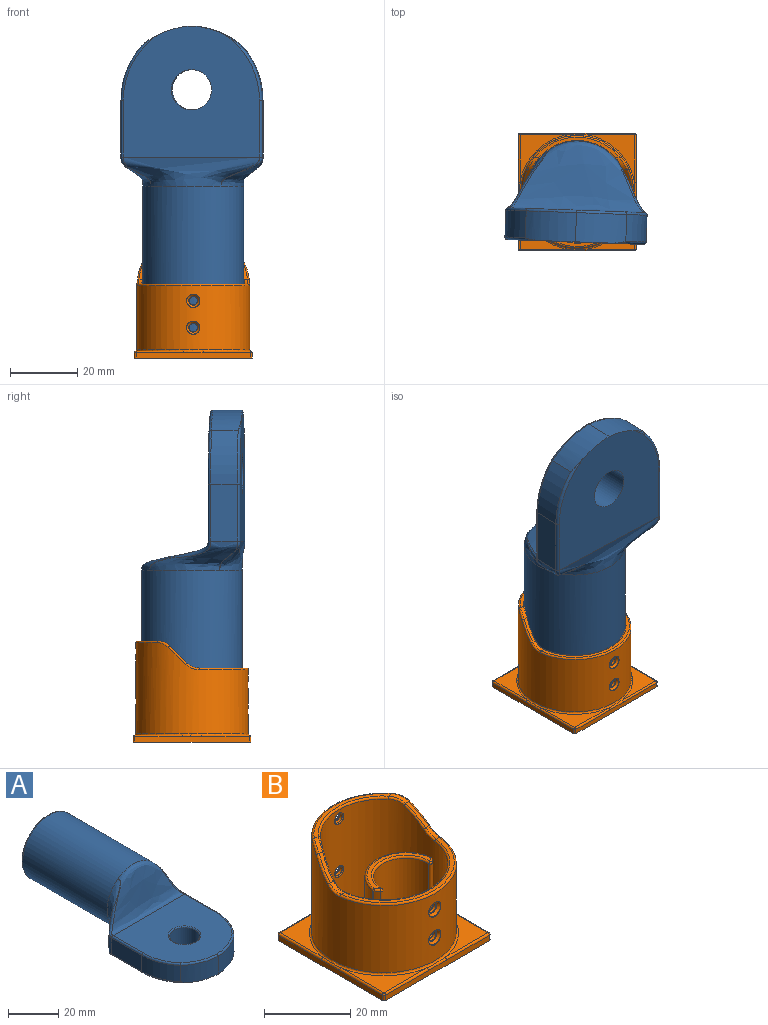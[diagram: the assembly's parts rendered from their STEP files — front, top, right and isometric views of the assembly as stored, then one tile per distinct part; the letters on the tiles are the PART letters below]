
ASSEMBLY  parts=2 mates=1
PART A: 36 faces, bbox 46x98x32.5 mm
  f0: plane 40.51x38.23mm, normal (0,0,1), area 1235.7mm2, adj f8,f9,f10,f11,f12,f13,f19,f29
  f1: plane 40.51x38.98mm, normal (0,0,-1), area 1275.2mm2, adj f5,f6,f14,f15,f16,f17,f18,f31
  f2: plane 16.95x7.94mm, normal (1,0,0), area 134.5mm2, adj f7,f13,f16,f30
  f3: plane 16.95x7.94mm, normal (-1,0,0), area 134.5mm2, adj f4,f8,f14,f28
  f4: cylinder r=24.27mm len=16.02mm, axis (0,0,-1), area 138.9mm2, adj f3,f5,f9,f15
  f5: cylinder r=24.27mm len=14.96mm, axis (0,0,-1), area 140.6mm2, adj f1,f4,f6,f10,f15
  f6: cylinder r=24.27mm len=14.96mm, axis (0,0,-1), area 140.6mm2, adj f1,f5,f7,f11,f17
  f7: cylinder r=24.27mm len=16.02mm, axis (0,0,1), area 138.9mm2, adj f2,f6,f12,f17
  f8: cylinder r=0.75mm len=16.95mm, axis (0,-1,0), area 19.8mm2, adj f0,f3,f9,f33
  f9: torus R=23.53mm, axis (0,0,1), area 20.2mm2, adj f0,f4,f8,f10
  f10: torus R=23.53mm, axis (0,0,1), area 19mm2, adj f0,f5,f9,f11
  f11: torus R=23.53mm, axis (0,0,1), area 19mm2, adj f0,f6,f10,f12
  f12: torus R=23.53mm, axis (0,0,1), area 20.2mm2, adj f0,f7,f11,f13
  f13: cylinder r=0.75mm len=16.95mm, axis (0,1,0), area 19.8mm2, adj f0,f2,f12,f32
  f14: cylinder r=0.75mm len=16.95mm, axis (0,1,0), area 19.8mm2, adj f1,f3,f15,f27,f28,f31
  f15: torus R=23.53mm, axis (0,0,1), area 23.6mm2, adj f1,f4,f5,f14
  f16: cylinder r=0.75mm len=16.95mm, axis (0,-1,0), area 19.8mm2, adj f1,f2,f17,f20,f30,f31
  f17: torus R=23.53mm, axis (0,0,1), area 23.6mm2, adj f1,f6,f7,f16
  f18: cylinder r=6mm len=12mm, axis (0,0,1), area 336.6mm2, adj f1,f19
  f19: torus R=6.5mm, axis (0,0,1), area 30.5mm2, adj f0,f18
  f20: plane 0.77x0.77mm, normal (0,-1,0), area 0mm2, adj f16,f34
  f21: plane 28.51x28.51mm, normal (0,1,0), area 147.8mm2, adj f25,f26
  f22: cylinder r=15mm len=47.63mm, axis (0,1,0), area 4489.2mm2, adj f26,f28,f29,f30,f31
  f23: cylinder r=11.75mm len=44.25mm, axis (0,1,0), area 3267.2mm2, adj f24,f25
  f24: plane 23.5x23.5mm, normal (0,1,0), area 433.7mm2, adj f23
  f25: torus R=12.5mm, axis (0,1,0), area 88.4mm2, adj f21,f23
  f26: torus R=14.25mm, axis (0,1,0), area 108.4mm2, adj f21,f22
  f27: plane 0.77x0.77mm, normal (0,-1,0), area 0mm2, adj f14,f35
  f28: bspline ~27.21x12.28mm, area 160.6mm2, adj f3,f14,f22,f29,f31,f33,f35
  f29: bspline ~42x20.82mm, area 655.7mm2, adj f0,f22,f28,f30,f32,f33
  f30: bspline ~23.72x12.28mm, area 172.3mm2, adj f2,f16,f22,f29,f31,f32,f34
  f31: bspline ~42x8.62mm, area 297.2mm2, adj f1,f14,f16,f22,f28,f30,f34,f35
  f32: bspline ~15.03x8.79mm, area 23.9mm2, adj f13,f29,f30
  f33: bspline ~18.51x12.27mm, area 21.4mm2, adj f8,f28,f29
  f34: bspline ~12.27x8.29mm, area 7.3mm2, adj f20,f30,f31
  f35: bspline ~8.76x8.34mm, area 5.5mm2, adj f27,f28,f31
PART B: 130 faces, bbox 38.1x38.1x30.6 mm
  f0: cylinder r=14.75mm len=29.5mm, axis (0,0,-1), area 2083.4mm2, adj f1,f93,f94,f95,f96,f97,f98,f99
  f1: bspline ~3x2.95mm, area 3.2mm2, adj f0,f2
  f2: cylinder r=1.25mm len=2.5mm, axis (0,1,0), area 6.1mm2, adj f1,f3
  f3: torus R=1.5mm, axis (0,-1,0), area 1.6mm2, adj f2,f4
  f4: cone r=1.25mm half-angle=45deg, axis (0,1,0), area 9.2mm2, adj f3,f5,f88,f89,f90,f91,f92
  f5: bspline ~1.97x1.65mm, area 0.2mm2, adj f4,f6,f92
  f6: cylinder r=16.75mm len=33.5mm, axis (0,0,-1), area 2309.1mm2, adj f5,f7,f13,f14,f15,f16,f17,f18
  f7: cylinder r=2mm len=1.48mm, axis (0,-1,0), area 0mm2, adj f6,f8
  f8: torus R=1.75mm, axis (0,-1,0), area 0.3mm2, adj f7,f9,f13,f17
  f9: cone r=1.25mm half-angle=45deg, axis (0,-1,0), area 9.2mm2, adj f8,f10,f11,f13,f14,f16,f17
  f10: torus R=1.75mm, axis (0,-1,0), area 0.3mm2, adj f9,f14,f15,f16
  f11: torus R=1.5mm, axis (0,1,0), area 1.6mm2, adj f9,f12
  f12: cylinder r=1.25mm len=2.5mm, axis (0,-1,0), area 6.1mm2, adj f11,f95
  f13: bspline ~1.97x1.65mm, area 0.2mm2, adj f6,f8,f9
  f14: bspline ~1.97x1.65mm, area 0.2mm2, adj f6,f9,f10
  f15: cylinder r=2mm len=1.48mm, axis (0,-1,0), area 0mm2, adj f6,f10
  f16: bspline ~1.97x1.65mm, area 0.2mm2, adj f6,f9,f10
  f17: bspline ~1.97x1.65mm, area 0.2mm2, adj f6,f8,f9
  f18: cylinder r=2mm len=1.48mm, axis (0,1,0), area 0mm2, adj f6,f19
  f19: torus R=1.75mm, axis (0,1,0), area 0.3mm2, adj f18,f20,f24,f28
  f20: cone r=1.25mm half-angle=45deg, axis (0,1,0), area 9.2mm2, adj f19,f21,f22,f24,f25,f27,f28
  f21: torus R=1.75mm, axis (0,1,0), area 0.3mm2, adj f20,f25,f26,f27
  f22: torus R=1.5mm, axis (0,-1,0), area 1.6mm2, adj f20,f23
  f23: cylinder r=1.25mm len=2.5mm, axis (0,1,0), area 6.1mm2, adj f22,f93
  f24: bspline ~1.97x1.65mm, area 0.2mm2, adj f6,f19,f20
  f25: bspline ~1.97x1.65mm, area 0.2mm2, adj f6,f20,f21
  f26: cylinder r=2mm len=1.48mm, axis (0,1,0), area 0mm2, adj f6,f21
  f27: bspline ~1.97x1.65mm, area 0.2mm2, adj f6,f20,f21
  f28: bspline ~1.97x1.65mm, area 0.2mm2, adj f6,f19,f20
  f29: cylinder r=2mm len=1.48mm, axis (0,1,0), area 0mm2, adj f6,f89
  f30: cylinder r=2mm len=1.48mm, axis (0,1,0), area 0mm2, adj f6,f92
  f31: cylinder r=2mm len=1.48mm, axis (0,-1,0), area 0mm2, adj f6,f32
  f32: torus R=1.75mm, axis (0,-1,0), area 0.3mm2, adj f31,f33,f37,f41
  f33: cone r=1.25mm half-angle=45deg, axis (0,-1,0), area 9.2mm2, adj f32,f34,f35,f37,f38,f40,f41
  f34: torus R=1.75mm, axis (0,-1,0), area 0.3mm2, adj f33,f38,f39,f40
  f35: torus R=1.5mm, axis (0,1,0), area 1.6mm2, adj f33,f36
  f36: cylinder r=1.25mm len=2.5mm, axis (0,-1,0), area 6.1mm2, adj f35,f94
  f37: bspline ~1.97x1.65mm, area 0.2mm2, adj f6,f32,f33
  f38: bspline ~1.97x1.65mm, area 0.2mm2, adj f6,f33,f34
  f39: cylinder r=2mm len=1.48mm, axis (0,-1,0), area 0mm2, adj f6,f34
  f40: bspline ~1.97x1.65mm, area 0.2mm2, adj f6,f33,f34
  f41: bspline ~1.97x1.65mm, area 0.2mm2, adj f6,f32,f33
  f42: bspline ~10.08x10.01mm, area 6.5mm2, adj f6,f43,f81,f87
  f43: plane 5.07x5.07mm, normal (0,-0.71,0.71), area 7.5mm2, adj f42,f44,f50,f99
  f44: cylinder r=5mm len=3.54mm, axis (-1,0,0), area 4.7mm2, adj f43,f45,f87,f98
  f45: plane 25.51x6.18mm, normal (0,0,1), area 27.6mm2, adj f44,f46,f86,f97
  f46: cylinder r=5mm len=3.54mm, axis (-1,0,0), area 4.7mm2, adj f45,f47,f85,f96
  f47: plane 5.07x5.07mm, normal (0,-0.71,0.71), area 7.5mm2, adj f46,f48,f84,f129
  f48: cylinder r=5mm len=3.54mm, axis (-1,0,0), area 4mm2, adj f47,f49,f83,f128
  f49: plane 32.24x14.18mm, normal (0,0,1), area 45.3mm2, adj f48,f50,f82,f127
  f50: cylinder r=5mm len=3.54mm, axis (-1,0,0), area 4mm2, adj f43,f49,f81,f126
  f51: torus R=17.25mm, axis (0,0,1), area 81.7mm2, adj f6,f52,f74,f75,f76,f77,f78,f79
  f52: plane 14.07x14.07mm, normal (0,0,1), area 56.3mm2, adj f51,f53,f73
  f53: cylinder r=0.5mm len=14.07mm, axis (1,0,0), area 11.1mm2, adj f52,f54,f72,f74
  f54: plane 34x1.53mm, normal (0,1,0), area 51.1mm2, adj f53,f55,f69,f70,f71,f74
  f55: cylinder r=0.5mm len=14.07mm, axis (1,0,0), area 11.1mm2, adj f54,f56,f74,f75
  f56: sphere r=0.5mm, area 0.5mm2, adj f55,f57,f69
  f57: cylinder r=0.5mm len=14.07mm, axis (0,1,0), area 11.1mm2, adj f56,f58,f75,f76
  f58: plane 34x1.53mm, normal (-1,0,0), area 51.1mm2, adj f57,f59,f68,f69,f70,f76
  f59: cylinder r=0.5mm len=14.07mm, axis (0,1,0), area 11.1mm2, adj f58,f60,f76,f77
  f60: sphere r=0.5mm, area 0.4mm2, adj f59,f61,f68
  f61: cylinder r=0.5mm len=14.07mm, axis (-1,0,0), area 11.1mm2, adj f60,f62,f77,f78
  f62: plane 34x1.53mm, normal (0,-1,0), area 51.1mm2, adj f61,f63,f67,f68,f70,f78
  f63: cylinder r=0.5mm len=14.07mm, axis (-1,0,0), area 11.1mm2, adj f62,f64,f78,f79
  f64: sphere r=0.5mm, area 0.4mm2, adj f63,f65,f67
  f65: cylinder r=0.5mm len=14.07mm, axis (0,-1,0), area 11.1mm2, adj f64,f66,f79,f80
  f66: plane 34x1.53mm, normal (1,0,0), area 51.1mm2, adj f65,f67,f70,f71,f73,f80
  f67: cylinder r=0.5mm len=1.5mm, axis (0,0,1), area 1.2mm2, adj f62,f64,f66,f70
  f68: cylinder r=0.5mm len=1.5mm, axis (0,0,-1), area 1.2mm2, adj f58,f60,f62,f70
  f69: cylinder r=0.5mm len=1.5mm, axis (0,0,1), area 1.2mm2, adj f54,f56,f58,f70
  f70: plane 35x35mm, normal (0,0,-1), area 1224.8mm2, adj f54,f58,f62,f66,f67,f68,f69,f71
  f71: cylinder r=0.5mm len=1.5mm, axis (0,0,-1), area 1.2mm2, adj f54,f66,f70,f72
  f72: sphere r=0.5mm, area 0.2mm2, adj f53,f71,f73
  f73: cylinder r=0.5mm len=14.07mm, axis (0,-1,0), area 11.1mm2, adj f52,f66,f72,f80
  f74: bspline ~6.69x0.57mm, area 4.1mm2, adj f51,f53,f54,f55
  f75: plane 14.07x14.07mm, normal (0,0,1), area 56.3mm2, adj f51,f55,f57
  f76: bspline ~8.52x0.68mm, area 4.1mm2, adj f51,f57,f58,f59
  f77: plane 14.07x14.07mm, normal (0,0,1), area 56.3mm2, adj f51,f59,f61
  f78: bspline ~8.52x0.68mm, area 4.1mm2, adj f51,f61,f62,f63
  f79: plane 14.07x14.07mm, normal (0,0,1), area 56.3mm2, adj f51,f63,f65
  f80: bspline ~6.19x0.52mm, area 4.1mm2, adj f51,f65,f66,f73
  f81: bspline ~6.07x2.88mm, area 3.3mm2, adj f6,f42,f50,f82
  f82: torus R=16.25mm, axis (0,0,1), area 37.6mm2, adj f6,f49,f81,f83
  f83: bspline ~6.07x2.88mm, area 3.3mm2, adj f6,f48,f82,f84
  f84: bspline ~10.08x10.01mm, area 6.5mm2, adj f6,f47,f83,f85
  f85: bspline ~4.84x3.15mm, area 3.8mm2, adj f6,f46,f84,f86
  f86: torus R=16.25mm, axis (0,0,1), area 23.5mm2, adj f6,f45,f85,f87
  f87: bspline ~5.75x3.9mm, area 3.8mm2, adj f6,f42,f44,f86
  f88: bspline ~1.97x1.65mm, area 0.2mm2, adj f4,f6,f89
  f89: torus R=1.75mm, axis (0,1,0), area 0.3mm2, adj f4,f29,f88,f90
  f90: bspline ~1.97x1.65mm, area 0.2mm2, adj f4,f6,f89
  f91: bspline ~1.97x1.65mm, area 0.2mm2, adj f4,f6,f92
  f92: torus R=1.75mm, axis (0,1,0), area 0.3mm2, adj f4,f5,f30,f91
  f93: bspline ~3x2.95mm, area 3.2mm2, adj f0,f23
  f94: bspline ~3x2.95mm, area 3.2mm2, adj f0,f36
  f95: bspline ~3x2.95mm, area 3.2mm2, adj f0,f12
  f96: bspline ~5.44x3.9mm, area 3mm2, adj f0,f46,f97,f129
  f97: torus R=15.25mm, axis (0,0,1), area 19.9mm2, adj f0,f45,f96,f98
  f98: bspline ~5.44x3.9mm, area 3mm2, adj f0,f44,f97,f99
  f99: bspline ~5.42x5.2mm, area 5mm2, adj f0,f43,f98,f126
  f100: plane 29.5x29.5mm, normal (0,0,1), area 601.2mm2, adj f0,f101,f119,f120,f121,f122,f123,f124
  f101: torus R=1mm, axis (0,0,1), area 0.4mm2, adj f100,f102,f119,f125
  f102: cylinder r=0.5mm len=19mm, axis (0,0,-1), area 7mm2, adj f101,f103,f117,f118
  f103: cylinder r=9.5mm len=19mm, axis (0,0,-1), area 517.1mm2, adj f102,f104,f116,f119
  f104: torus R=9mm, axis (0,0,1), area 21mm2, adj f103,f105,f115,f118
  f105: plane 17.83x9.05mm, normal (0,0,1), area 25.4mm2, adj f104,f106,f113,f114
  f106: torus R=10.75mm, axis (0,0,1), area 1.2mm2, adj f105,f107,f117,f118
  f107: sphere r=0.5mm, area 0.5mm2, adj f106,f108,f113
  f108: cylinder r=0.5mm len=19mm, axis (0,0,1), area 22.8mm2, adj f107,f109,f117,f124
  f109: cylinder r=7.5mm len=19mm, axis (0,0,-1), area 445.2mm2, adj f108,f110,f113,f123
  f110: cylinder r=0.5mm len=19mm, axis (0,0,1), area 22.8mm2, adj f109,f111,f112,f122
  f111: cylinder r=11.25mm len=19mm, axis (0,0,-1), area 29.6mm2, adj f110,f114,f116,f121
  f112: sphere r=0.5mm, area 0.6mm2, adj f110,f113,f114
  f113: torus R=8mm, axis (0,0,1), area 18.8mm2, adj f105,f107,f109,f112
  f114: torus R=10.75mm, axis (0,0,1), area 1.2mm2, adj f105,f111,f112,f115
  f115: sphere r=0.5mm, area 0.2mm2, adj f104,f114,f116
  f116: cylinder r=0.5mm len=19mm, axis (0,0,-1), area 7mm2, adj f103,f111,f115,f120
  f117: cylinder r=11.25mm len=19mm, axis (0,0,-1), area 29.6mm2, adj f102,f106,f108,f125
  f118: sphere r=0.5mm, area 0.2mm2, adj f102,f104,f106
  f119: torus R=10mm, axis (0,0,1), area 21.8mm2, adj f100,f101,f103,f120
  f120: torus R=1mm, axis (0,0,1), area 0.4mm2, adj f100,f116,f119,f121
  f121: torus R=11.75mm, axis (0,0,1), area 1.2mm2, adj f100,f111,f120,f122
  f122: torus R=1mm, axis (0,0,1), area 1.3mm2, adj f100,f110,f121,f123
  f123: torus R=7mm, axis (0,0,1), area 18mm2, adj f100,f109,f122,f124
  f124: torus R=1mm, axis (0,0,1), area 1.3mm2, adj f100,f108,f123,f125
  f125: torus R=11.75mm, axis (0,0,1), area 1.2mm2, adj f100,f101,f117,f124
  f126: bspline ~5.69x2.84mm, area 3.1mm2, adj f0,f50,f99,f127
  f127: torus R=15.25mm, axis (0,0,1), area 33.6mm2, adj f0,f49,f126,f128
  f128: bspline ~5.69x2.84mm, area 3.1mm2, adj f0,f48,f127,f129
  f129: bspline ~5.42x5.2mm, area 5mm2, adj f0,f47,f96,f128
PLACE A rot(axis=(-1,0.02,-0.02),90deg) t=(-0.53,-14.99,6.21)mm
PLACE B at identity fixed
MATE cylindrical A.f25 <-> B.f0  axis (0,0,-1) through (0,0,3.5)mm
